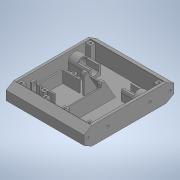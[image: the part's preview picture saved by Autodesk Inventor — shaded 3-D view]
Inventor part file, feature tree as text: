
AUTODESK INVENTOR PART (.ipt)
format: ipt  version: 2020 (Build 240168000, 168)  size: 649,728 bytes
history: native  units: in
note: dims shown in document units (in); Inventor stores cm internally (conversion verified against a paired STEP export)
features: extrude x19, sketch x19, projected_geometry x14, mirror x6, plane x1
ambient origin geometry x8: Origin, YZ Plane, XZ Plane, XY Plane, X Axis, Y Axis, Z Axis, Center Point
bodies: Solid1 (feature_tree)
feature tree (59):
  extrude  "Extrusion1"  Depth=5.9055in
  extrude  "Extrusion2"  TaperAngle=0.0deg  [1 undecoded]
  extrude  "Extrusion3"  Depth=1.063in
  extrude  "Extrusion4"  Depth=0.315in
  extrude  "Extrusion5"  TaperAngle=0.0deg  [1 undecoded]
  extrude  "Extrusion6"  Depth=0.5906in
  mirror  "Mirror1"
  extrude  "Extrusion7"  Depth=0.0787in
  mirror  "Mirror2"
  extrude  "Extrusion8"  Depth=0.6102in
  mirror  "Mirror3"
  plane  "Work Plane1"
  extrude  "Extrusion9"  Depth=0.7874in TaperAngle=0.0deg
  mirror  "Mirror4"
  extrude  "Extrusion10"  Depth=6.063in TaperAngle=0.0deg
  extrude  "Extrusion11"  Depth=0.1575in
  extrude  "Extrusion12"  TaperAngle=0.0deg  [1 undecoded]
  extrude  "Extrusion13"  Depth=0.2756in
  extrude  "Extrusion14"  Depth=0.4331in
  extrude  "Extrusion17"  Depth=2.7559in
  extrude  "Extrusion18"  Depth=0.0453in
  mirror  "Mirror6"
  extrude  "Extrusion19"  TaperAngle=0.0deg  [1 undecoded]
  mirror  "Mirror7"
  extrude  "Extrusion20"  Depth=0.0787in
  extrude  "Extrusion21"  Depth=0.993in
  sketch  "Sketch1"  dims[d0=1.1811in d1=5.9055in]
  sketch  "Sketch2"  dims[d2=5.1181in d3=0.0in]
  projected_geometry  "Projected Loop1"
  sketch  "Sketch3"  dims[d4=0.1575in d5=1.063in]
  projected_geometry  "Projected Loop2"
  projected_geometry  "Projected Loop3"
  sketch  "Sketch4"  dims[d6=0.0in d8=0.315in]
  sketch  "Sketch5"  dims[d10=0.993in d11=0.0in]
  projected_geometry  "Projected Loop4"
  sketch  "Sketch6"  dims[d12=0.6496in d13=0.5906in]
  sketch  "Sketch7"  dims[d14=1.5748in d15=0.0787in]
  sketch  "Sketch9"  dims[d16=0.5512in d17=0.0in d18=0.6102in]
  sketch  "Sketch10"  dims[d19=0.4803in d20=0.7874in d21=0.0in]
  sketch  "Sketch12"  dims[d22=0.1654in d23=6.063in d24=0.0in]
  projected_geometry  "Projected Loop6"
  projected_geometry  "Projected Loop7"
  projected_geometry  "Projected Loop8"
  sketch  "Sketch13"  dims[d25=0.5114in d26=0.1575in]
  sketch  "Sketch14"  dims[d27=1.5748in d28=0.0in d29=0.0in]
  sketch  "Sketch15"  dims[d30=0.1575in d31=0.2756in]
  projected_geometry  "Projected Loop15"
  sketch  "Sketch16"  dims[d32=0.0in d33=0.4331in]
  projected_geometry  "Projected Loop19"
  projected_geometry  "Projected Loop20"
  projected_geometry  "Projected Loop21"
  projected_geometry  "Projected Loop22"
  projected_geometry  "Projected Loop23"
  projected_geometry  "Projected Loop24"
  sketch  "Sketch20"  dims[d34=0.0906in d38=2.7559in]
  sketch  "Sketch21"  dims[d40=0.0453in d41=0.0909in]
  sketch  "Sketch22"  dims[d42=0.2362in d43=0.0in]
  sketch  "Sketch23"  dims[d44=60.0deg d45=0.0787in]
  sketch  "Sketch25"  dims[d46=0.315in d48=0.993in d49=0.0in d53=0.2756in d54=0.0in d55=0.4724in d56=1.1811in d57=1.5748in d58=1.5748in d59=0.0787in d60=0.0787in d62=0.315in d63=0.7677in d64=0.0in d66=0.1476in d67=0.2756in d68=0.0in d69=0.7874in d70=0.2953in d71=0.1181in d72=0.0in d89=0.0157in d90=0.0157in d91=0.1476in d92=0.1476in d96=0.315in d97=0.1575in d98=0.1181in d99=0.0in d102=0.1772in d104=0.3346in d105=135.0deg d106=0.2362in d107=0.0in d108=0.0394in d109=0.0in d110=0.063in d111=0.0394in d112=0.0in d117=0.993in d118=0.063in d119=0.3937in d120=0.0in]
note: 4 required parameter values undecoded (feature->parameter linkage not recoverable at this tier; creation-order binding heuristic only, values carry confidence <= 0.55)
